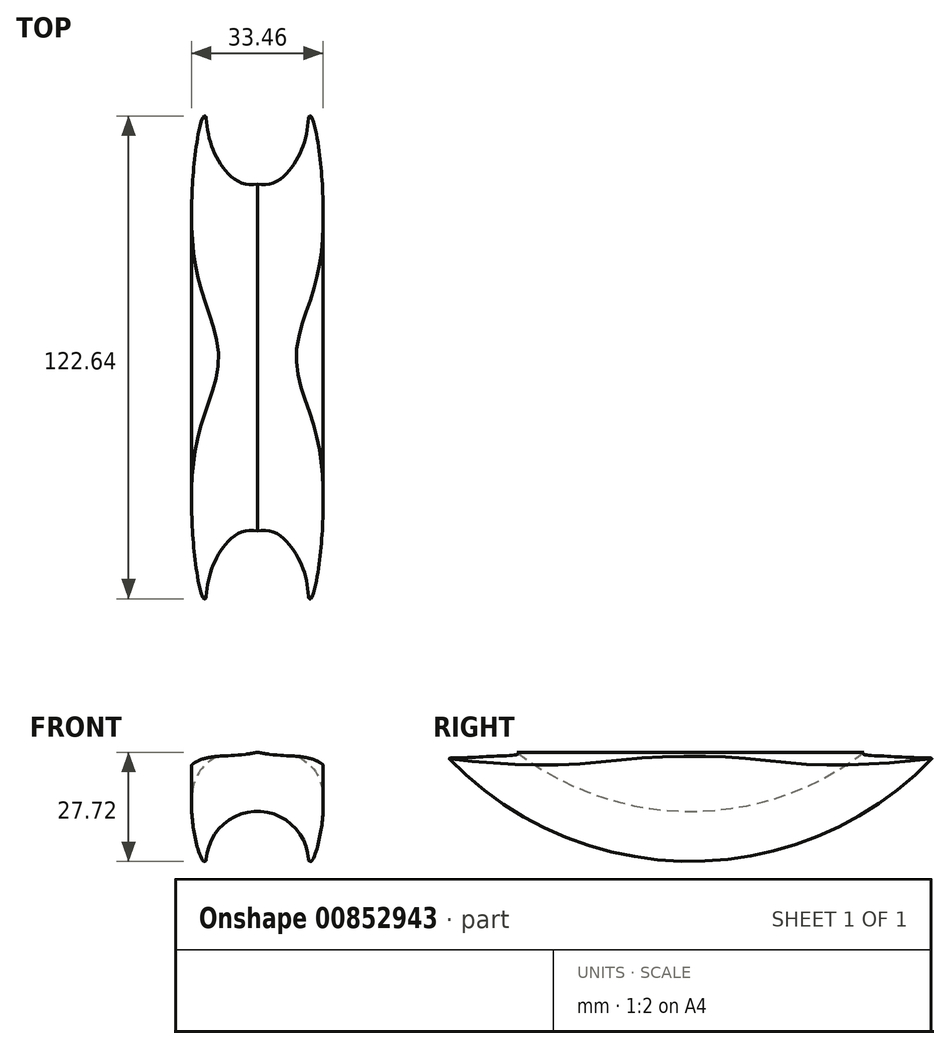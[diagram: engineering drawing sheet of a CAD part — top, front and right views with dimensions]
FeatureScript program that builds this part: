
annotation { "Feature Type Name" : "Feature", "Feature Type Description" : "" }
export const myFeature = defineFeature(function(context is Context, id is Id, definition is map)
    precondition{}
    {
        {
            var Q0;
            Q0=qCreatedBy(makeId("Front.planeOp"),FACE);
            var sketch = newSketch(context, id + "F0", { "sketchPlane" : qUnion([Q0])});
            skArc(sketch, "E0", {"start": v(-13, 0) * mm, "mid": v(0, 13) * mm, "end": v(13, 0) * mm});
            skPoint(sketch, "E1", {"position": v(0, 13) * mm});
            skLineSegment(sketch, "E2", {"start": v(0, 13) * mm, "end": v(0, 85.3) * mm});
            skPoint(sketch, "E3", {"position": v(0, 85.3) * mm});
            skFitSpline(sketch, "E4", {"points": [v(-13, 0) * mm, v(-16.3, 19.24) * mm, v(0, 29) * mm], "startDerivative": vector(-9.29, -6.85) * mm, "endDerivative": vector(49.75, 3.75) * mm});
            skFitSpline(sketch, "E5.MirrorCS", {"points": [v(13, 0) * mm, v(16.3, 19.24) * mm, v(0, 29) * mm], "startDerivative": vector(9.29, -6.85) * mm, "endDerivative": vector(-49.75, 3.75) * mm});
            skSolve(sketch);
        }
        {
            var Q0;
            Q0=qCreatedBy(makeId("Right.planeOp"),FACE);
            var sketch = newSketch(context, id + "F1", { "sketchPlane" : qUnion([Q0])});
            skPoint(sketch, "E6.0", {"position": v(0, 85.3) * mm});
            skPoint(sketch, "E7.0", {"position": v(0, 13) * mm});
            skCircle(sketch, "E8", {"center": v(0, 85.3) * mm, "radius": 72.3 * mm});
            skSolve(sketch);
        }
        {
            var Q0;
            {var subQ0=sQuery(id+"F0.wireOp",EDGE,"E4");Q0=makeQuery(id+"F0.imprint","IMPRINT",FACE,{"disambiguationData":[TD([[makeQuery(id+"F0.imprint","IMPRINT",EDGE,{"derivedFrom":subQ0}),-1.0]])]});}
            var Q1;
            {var subQ0=sQuery(id+"F0.wireOp",EDGE,"E5.MirrorCS");Q1=makeQuery(id+"F0.imprint","IMPRINT",FACE,{"disambiguationData":[TD([[makeQuery(id+"F0.imprint","IMPRINT",EDGE,{"derivedFrom":subQ0}),1.0]])]});}
            var Q2;
            Q2=sQuery(id+"F1.wireOp",EDGE,"E8");
            revolve(context, id + "F2", {"surfaceOperationType" : NewSurfaceOperationType.NEW, "entities" : qUnion([Q0, Q1]), "axis" : qUnion([Q2]), "revolveType" : RevolveType.SYMMETRIC, "angle" : 110 * degree});
        }
        {
            var Q0;
            Q0=qCreatedBy(makeId("Front.planeOp"),FACE);
            var sketch = newSketch(context, id + "F3", { "sketchPlane" : qUnion([Q0])});
            skFitSpline(sketch, "E9.0", {"points": [v(13, 0) * mm, v(14.54, -1.14) * mm, v(18.53, 22.3) * mm, v(6.68, 27.16) * mm, v(0, 28) * mm]});
            skFitSpline(sketch, "E10.0", {"points": [v(-13, 0) * mm, v(-14.54, -1.14) * mm, v(-18.53, 22.3) * mm, v(-6.68, 27.16) * mm, v(0, 28) * mm]});
            skArc(sketch, "E11.0", {"start": v(-13, 0) * mm, "mid": v(0, 13) * mm, "end": v(13, 0) * mm});
            skSolve(sketch);
        }
        {
            var Q0;
            Q0 = qSketchRegion(id + "F3", true);
            extrude(context, id + "F4", {"entities" : qUnion([Q0]), "operationType" : NewBodyOperationType.INTERSECT, "oppositeDirection" : true, "depth" : 100 * mm, "offsetDistance" : 25 * mm, "hasSecondDirection" : true, "secondDirectionOppositeDirection" : false, "secondDirectionDepth" : 100 * mm});
        }
        {
            var Q0;
            Q0=makeQuery(id+"F4.boolean.opBoolean","INTERSECT",EDGE,{"disambiguationData":[OD(1.0)],"derivedFrom":[makeQuery(id+"F2.opRevolve","SWEPT_FACE",FACE,{"disambiguationData":[OSD([sQuery(id+"F0.wireOp",EDGE,"E0")])]}),makeQuery(id+"F4.boolean.toolComplement.opBoolean","COPY",FACE,{"derivedFrom":makeQuery(id+"F4.opExtrude","SWEPT_FACE",FACE,{"disambiguationData":[OSD([sQuery(id+"F3.wireOp",EDGE,"E9.0")])]})})]});
            var Q1;
            Q1=makeQuery(id+"F4.boolean.opBoolean","INTERSECT",EDGE,{"disambiguationData":[OD(1.0)],"derivedFrom":[makeQuery(id+"F2.opRevolve","SWEPT_FACE",FACE,{"disambiguationData":[OSD([sQuery(id+"F0.wireOp",EDGE,"E0")])]}),makeQuery(id+"F4.boolean.toolComplement.opBoolean","COPY",FACE,{"derivedFrom":makeQuery(id+"F4.opExtrude","SWEPT_FACE",FACE,{"disambiguationData":[OSD([sQuery(id+"F3.wireOp",EDGE,"E10.0")])]})})]});
            var Q2;
            Q2=makeQuery(id+"F2.opRevolve","SWEPT_EDGE",EDGE,{"disambiguationData":[OSD([sQuery(id+"F0.wireOp",EDGE,"E0"),sQuery(id+"F0.wireOp",EDGE,"E5.MirrorCS")])]});
            var Q3;
            Q3=makeQuery(id+"F2.opRevolve","SWEPT_EDGE",EDGE,{"disambiguationData":[OSD([sQuery(id+"F0.wireOp",EDGE,"E0"),sQuery(id+"F0.wireOp",EDGE,"E4")])]});
            var Q4;
            Q4=makeQuery(id+"F4.boolean.opBoolean","INTERSECT",EDGE,{"disambiguationData":[OD(0.0)],"derivedFrom":[makeQuery(id+"F2.opRevolve","SWEPT_FACE",FACE,{"disambiguationData":[OSD([sQuery(id+"F0.wireOp",EDGE,"E0")])]}),makeQuery(id+"F4.boolean.toolComplement.opBoolean","COPY",FACE,{"derivedFrom":makeQuery(id+"F4.opExtrude","SWEPT_FACE",FACE,{"disambiguationData":[OSD([sQuery(id+"F3.wireOp",EDGE,"E9.0")])]})})]});
            var Q5;
            Q5=makeQuery(id+"F4.boolean.opBoolean","INTERSECT",EDGE,{"disambiguationData":[OD(0.0)],"derivedFrom":[makeQuery(id+"F2.opRevolve","SWEPT_FACE",FACE,{"disambiguationData":[OSD([sQuery(id+"F0.wireOp",EDGE,"E0")])]}),makeQuery(id+"F4.boolean.toolComplement.opBoolean","COPY",FACE,{"derivedFrom":makeQuery(id+"F4.opExtrude","SWEPT_FACE",FACE,{"disambiguationData":[OSD([sQuery(id+"F3.wireOp",EDGE,"E10.0")])]})})]});
            fillet(context, id + "F5", {"entities" : qUnion([Q0, Q1, Q2, Q3, Q4, Q5]), "radius" : 0.5 * mm, "tangentPropagation" : true, "allowEdgeOverflow" : false});
        }
    });
